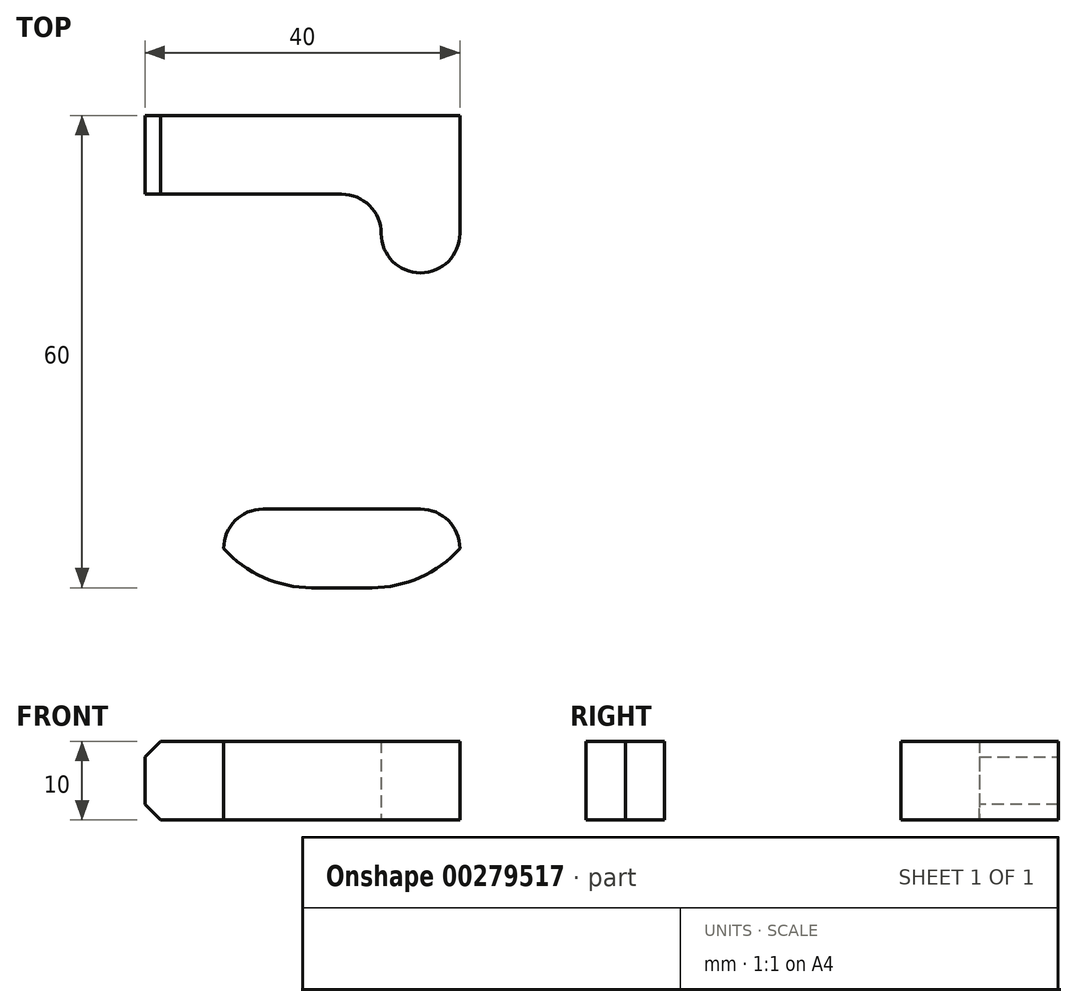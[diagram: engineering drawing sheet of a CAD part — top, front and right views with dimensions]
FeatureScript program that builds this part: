
annotation { "Feature Type Name" : "Feature", "Feature Type Description" : "" }
export const myFeature = defineFeature(function(context is Context, id is Id, definition is map)
    precondition{}
    {
        {
            var Q0;
            Q0=qCreatedBy(makeId("Top.planeOp"),FACE);
            var sketch = newSketch(context, id + "F0", { "sketchPlane" : qUnion([Q0])});
            skLineSegment(sketch, "E0.bottom", {"start": v(-34.5, 20.7) * mm, "end": v(-4.5, 20.7) * mm});
            skLineSegment(sketch, "E0.top", {"start": v(-34.5, 10.7) * mm, "end": v(-4.5, 10.7) * mm});
            skLineSegment(sketch, "E0.left", {"start": v(-34.5, 20.7) * mm, "end": v(-34.5, 10.7) * mm});
            skLineSegment(sketch, "E0.right", {"start": v(-4.5, 20.7) * mm, "end": v(-4.5, 10.7) * mm});
            skLineSegment(sketch, "E1.bottom", {"start": v(-4.5, 20.7) * mm, "end": v(5.5, 20.7) * mm});
            skLineSegment(sketch, "E1.top", {"start": v(-4.5, 0.7) * mm, "end": v(5.5, 0.7) * mm});
            skLineSegment(sketch, "E1.left", {"start": v(-4.5, 20.7) * mm, "end": v(-4.5, 0.7) * mm});
            skLineSegment(sketch, "E1.right", {"start": v(5.5, 20.7) * mm, "end": v(5.5, 0.7) * mm});
            skLineSegment(sketch, "E2.bottom", {"start": v(-34.5, 10.7) * mm, "end": v(-24.5, 10.7) * mm});
            skLineSegment(sketch, "E2.top", {"start": v(-34.5, -39.3) * mm, "end": v(-24.5, -39.3) * mm});
            skLineSegment(sketch, "E2.left", {"start": v(-34.5, 10.7) * mm, "end": v(-34.5, -39.3) * mm});
            skLineSegment(sketch, "E2.right", {"start": v(-24.5, 10.7) * mm, "end": v(-24.5, -39.3) * mm});
            skLineSegment(sketch, "E3.bottom", {"start": v(-24.5, -39.3) * mm, "end": v(5.5, -39.3) * mm});
            skLineSegment(sketch, "E3.top", {"start": v(-24.5, -29.3) * mm, "end": v(5.5, -29.3) * mm});
            skLineSegment(sketch, "E3.left", {"start": v(-24.5, -39.3) * mm, "end": v(-24.5, -29.3) * mm});
            skLineSegment(sketch, "E3.right", {"start": v(5.5, -39.3) * mm, "end": v(5.5, -29.3) * mm});
            skLineSegment(sketch, "E4.bottom", {"start": v(5.5, -29.3) * mm, "end": v(-4.5, -29.3) * mm});
            skLineSegment(sketch, "E4.top", {"start": v(5.5, -19.3) * mm, "end": v(-4.5, -19.3) * mm});
            skLineSegment(sketch, "E4.left", {"start": v(5.5, -29.3) * mm, "end": v(5.5, -19.3) * mm});
            skLineSegment(sketch, "E4.right", {"start": v(-4.5, -29.3) * mm, "end": v(-4.5, -19.3) * mm});
            skSolve(sketch);
        }
        {
            var Q0;
            {var subQ1=sQuery(id+"F0.wireOp",EDGE,"E0.bottom");Q0=makeQuery(id+"F0.imprint","IMPRINT",FACE,{"disambiguationData":[TD([[makeQuery(id+"F0.imprint","IMPRINT",EDGE,{"derivedFrom":subQ1}),-1.0]])]});}
            var Q1;
            {var subQ3=sQuery(id+"F0.wireOp",EDGE,"E1.bottom");Q1=makeQuery(id+"F0.imprint","IMPRINT",FACE,{"disambiguationData":[TD([[makeQuery(id+"F0.imprint","IMPRINT",EDGE,{"derivedFrom":subQ3}),-1.0]])]});}
            var Q2;
            Q2=makeQuery(id+"F0.imprint","IMPRINT",FACE,{"disambiguationData":[TD([[makeQuery(id+"F0.imprint","IMPRINT",EDGE,{"derivedFrom":sQuery(id+"F0.wireOp",EDGE,"E4.bottom")}),-1.0]])]});
            var Q3;
            Q3=makeQuery(id+"F0.imprint","IMPRINT",FACE,{"disambiguationData":[TD([[makeQuery(id+"F0.imprint","IMPRINT",EDGE,{"derivedFrom":sQuery(id+"F0.wireOp",EDGE,"E2.bottom")}),-1.0]])]});
            var Q4;
            Q4=makeQuery(id+"F0.imprint","IMPRINT",FACE,{"disambiguationData":[TD([[makeQuery(id+"F0.imprint","IMPRINT",EDGE,{"derivedFrom":sQuery(id+"F0.wireOp",EDGE,"E3.bottom")}),1.0]])]});
            extrude(context, id + "F1", {"entities" : qUnion([Q0, Q1, Q2, Q3, Q4]), "depth" : 10 * mm});
        }
        {
            var Q0;
            Q0=makeQuery(id+"F1.opExtrude","SWEPT_EDGE",EDGE,{"disambiguationData":[OSD([sQuery(id+"F0.wireOp",EDGE,"E1.top"),sQuery(id+"F0.wireOp",EDGE,"E1.right")])]});
            var Q1;
            Q1=makeQuery(id+"F1.opExtrude","SWEPT_EDGE",EDGE,{"disambiguationData":[OSD([sQuery(id+"F0.wireOp",EDGE,"E1.top"),sQuery(id+"F0.wireOp",EDGE,"E1.left")])]});
            var Q2;
            Q2=makeQuery(id+"F1.opExtrude","SWEPT_EDGE",EDGE,{"disambiguationData":[OSD([sQuery(id+"F0.wireOp",EDGE,"E0.top"),sQuery(id+"F0.wireOp",EDGE,"E1.left")])]});
            var Q3;
            Q3=makeQuery(id+"F1.opExtrude","SWEPT_EDGE",EDGE,{"disambiguationData":[OSD([sQuery(id+"F0.wireOp",EDGE,"E4.top"),sQuery(id+"F0.wireOp",EDGE,"E4.left")])]});
            var Q4;
            Q4=makeQuery(id+"F1.opExtrude","SWEPT_EDGE",EDGE,{"disambiguationData":[OSD([sQuery(id+"F0.wireOp",EDGE,"E4.top"),sQuery(id+"F0.wireOp",EDGE,"E4.right")])]});
            var Q5;
            Q5=makeQuery(id+"F1.opExtrude","SWEPT_EDGE",EDGE,{"disambiguationData":[OSD([sQuery(id+"F0.wireOp",EDGE,"E0.top"),sQuery(id+"F0.wireOp",EDGE,"E2.bottom"),sQuery(id+"F0.wireOp",EDGE,"E2.right")])]});
            var Q6;
            Q6=makeQuery(id+"F1.opExtrude","SWEPT_EDGE",EDGE,{"disambiguationData":[OSD([sQuery(id+"F0.wireOp",EDGE,"E2.right"),sQuery(id+"F0.wireOp",EDGE,"E3.top"),sQuery(id+"F0.wireOp",EDGE,"E3.left")])]});
            var Q7;
            Q7=makeQuery(id+"F1.opExtrude","SWEPT_EDGE",EDGE,{"disambiguationData":[OSD([sQuery(id+"F0.wireOp",EDGE,"E3.top"),sQuery(id+"F0.wireOp",EDGE,"E4.bottom"),sQuery(id+"F0.wireOp",EDGE,"E4.right")])]});
            fillet(context, id + "F2", {"entities" : qUnion([Q0, Q1, Q2, Q3, Q4, Q5, Q6, Q7]), "radius" : 5 * mm, "tangentPropagation" : true, "allowEdgeOverflow" : false});
        }
        {
            var Q0;
            Q0=makeQuery(id+"F1.opExtrude","SWEPT_EDGE",EDGE,{"disambiguationData":[OSD([sQuery(id+"F0.wireOp",EDGE,"E0.bottom"),sQuery(id+"F0.wireOp",EDGE,"E0.left")])]});
            var Q1;
            Q1=makeQuery(id+"F1.opExtrude","SWEPT_EDGE",EDGE,{"disambiguationData":[OSD([sQuery(id+"F0.wireOp",EDGE,"E1.bottom"),sQuery(id+"F0.wireOp",EDGE,"E1.right")])]});
            var Q2;
            Q2=makeQuery(id+"F1.opExtrude","SWEPT_EDGE",EDGE,{"disambiguationData":[OSD([sQuery(id+"F0.wireOp",EDGE,"E3.bottom"),sQuery(id+"F0.wireOp",EDGE,"E3.right")])]});
            var Q3;
            Q3=makeQuery(id+"F1.opExtrude","SWEPT_EDGE",EDGE,{"disambiguationData":[OSD([sQuery(id+"F0.wireOp",EDGE,"E2.top"),sQuery(id+"F0.wireOp",EDGE,"E2.left")])]});
            fillet(context, id + "F3", {"entities" : qUnion([Q0, Q1, Q2, Q3]), "radius" : 15 * mm, "tangentPropagation" : true, "allowEdgeOverflow" : false});
        }
        {
            var Q0;
            Q0=makeQuery(id+"F1.opExtrude","CAP_EDGE",EDGE,{"disambiguationData":[OSD([sQuery(id+"F0.wireOp",EDGE,"E0.left"),sQuery(id+"F0.wireOp",EDGE,"E2.left")])],"isStart":false});
            var Q1;
            Q1=makeQuery(id+"F1.opExtrude","CAP_EDGE",EDGE,{"disambiguationData":[OSD([sQuery(id+"F0.wireOp",EDGE,"E0.left"),sQuery(id+"F0.wireOp",EDGE,"E2.left")])],"isStart":true});
            chamfer(context, id + "F4", {"entities" : qUnion([Q0, Q1]), "width" : 2 * mm, "tangentPropagation" : true});
        }
    });
